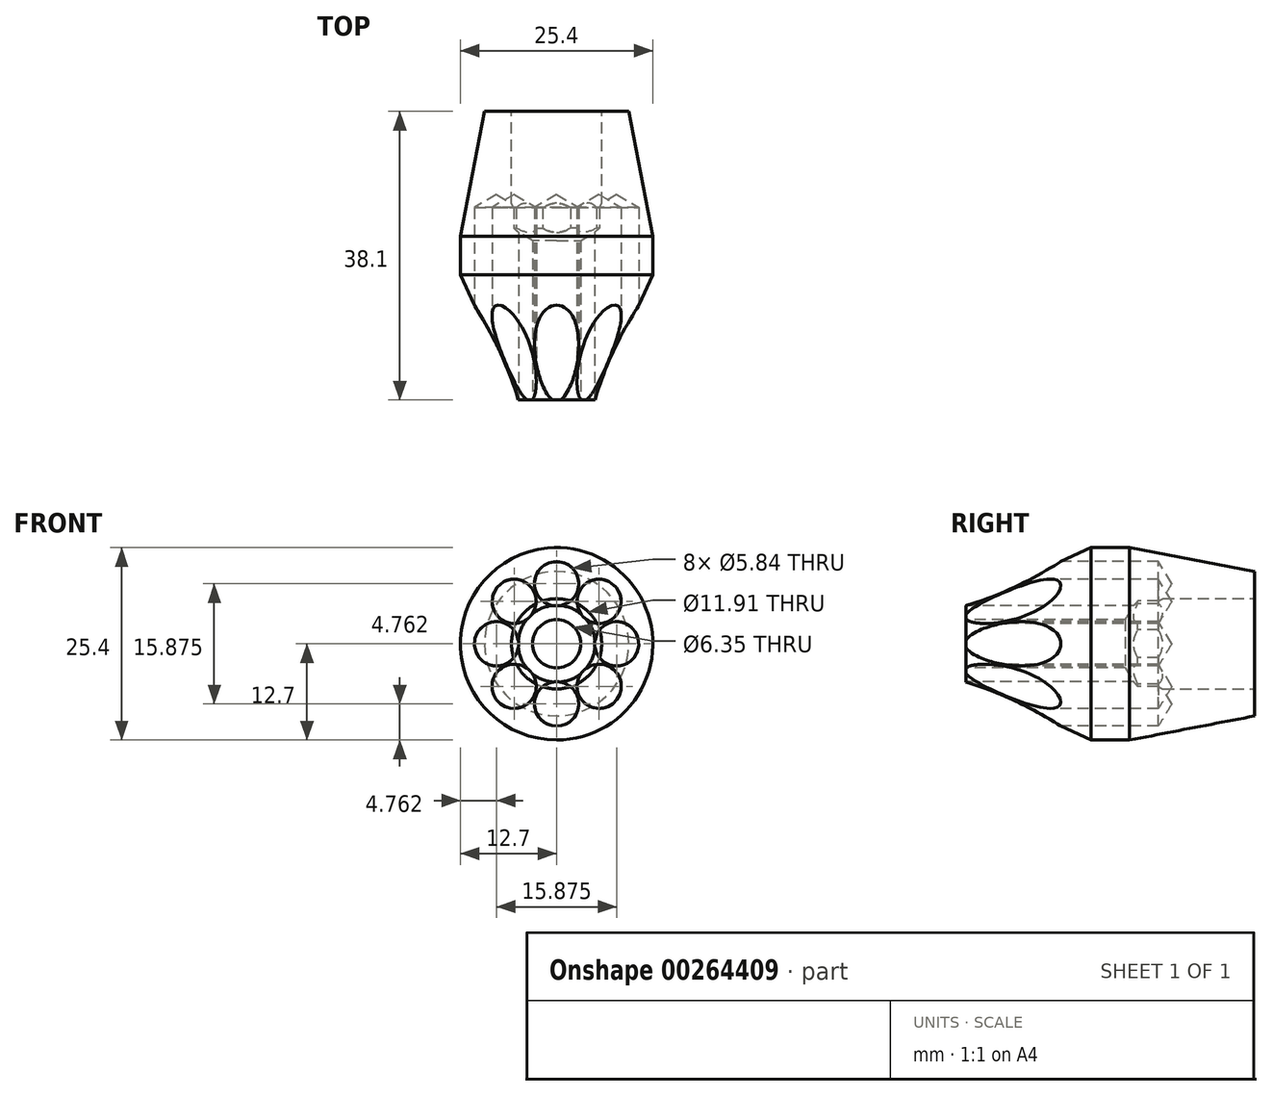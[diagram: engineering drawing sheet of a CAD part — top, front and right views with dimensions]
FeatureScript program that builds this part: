
annotation { "Feature Type Name" : "Feature", "Feature Type Description" : "" }
export const myFeature = defineFeature(function(context is Context, id is Id, definition is map)
    precondition{}
    {
        {
            var Q0;
            Q0=qCreatedBy(makeId("Front.planeOp"),FACE);
            var sketch = newSketch(context, id + "F0", { "sketchPlane" : qUnion([Q0])});
            skCircle(sketch, "E0", {"center": v(0, 0) * mm, "radius": 12.7 * mm});
            skSolve(sketch);
        }
        {
            var Q0;
            Q0 = qSketchRegion(id + "F0", true);
            extrude(context, id + "F1", {"entities" : qUnion([Q0]), "depth" : 38.1 * mm});
        }
        {
            var Q0;
            Q0=makeQuery(id+"F1.opExtrude","CAP_FACE",FACE,{"disambiguationData":[OSD([sQuery(id+"F0.wireOp",EDGE,"E0")])],"isStart":true});
            var sketch = newSketch(context, id + "F2", { "sketchPlane" : qUnion([Q0])});
            skPoint(sketch, "E1", {"position": v(0, 0) * mm});
            skSolve(sketch);
        }
        {
            var Q0;
            Q0=sQuery(id+"F2.wireOp",VERTEX,"E1");
            var Q1;
            Q1=makeQuery(id+"F1.opExtrude","SWEPT_BODY",BODY,{"disambiguationData":[OSD([sQuery(id+"F0.wireOp",EDGE,"E0")])]});
            hole(context, id + "F3", {"style" : HoleStyle.SIMPLE, "endStyle" : HoleEndStyle.BLIND, "standardTappedOrClearance" : lookupTablePath({ "standard" : "ANSI", "engagement" : "75%", "pitch" : "28 tpi", "size" : "1/2", "type" : "Tapped" }), "standardBlindInLast" : lookupTablePath({ "standard" : "ANSI", "engagement" : "75%", "pitch" : "28 tpi", "size" : "1/2", "type" : "Tapped" }), "holeDiameter" : 11.9 * mm, "showTappedDepth" : true, "holeDepth" : 15.42 * mm, "tappedDepth" : 12.7 * mm, "tapClearance" : 3, "locations" : qUnion([Q0]), "scope" : qUnion([Q1]), "majorDiameter" : 12.7 * mm});
        }
        {
            var Q0;
            Q0=makeQuery(id+"F1.opExtrude","CAP_FACE",FACE,{"disambiguationData":[OSD([sQuery(id+"F0.wireOp",EDGE,"E0")])],"isStart":false});
            var sketch = newSketch(context, id + "F4", { "sketchPlane" : qUnion([Q0])});
            skPoint(sketch, "E2", {"position": v(0, 0) * mm});
            skSolve(sketch);
        }
        {
            var Q0;
            Q0=sQuery(id+"F4.wireOp",VERTEX,"E2");
            var Q1;
            Q1=makeQuery(id+"F1.opExtrude","SWEPT_BODY",BODY,{"disambiguationData":[OSD([sQuery(id+"F0.wireOp",EDGE,"E0")])]});
            hole(context, id + "F5", {"style" : HoleStyle.SIMPLE, "endStyle" : HoleEndStyle.THROUGH, "holeDiameter" : 6.35 * mm, "tappedDepth" : 12.7 * mm, "tapClearance" : 3, "locations" : qUnion([Q0]), "scope" : qUnion([Q1])});
        }
        {
            var Q0;
            Q0=makeQuery(id+"F1.opExtrude","CAP_FACE",FACE,{"disambiguationData":[OSD([sQuery(id+"F0.wireOp",EDGE,"E0")])],"isStart":false});
            var sketch = newSketch(context, id + "F6", { "sketchPlane" : qUnion([Q0])});
            skLineSegment(sketch, "E3", {"start": v(0, 3.18) * mm, "end": v(0, 12.7) * mm});
            skCircle(sketch, "E4.cCircle", {"center": v(0, 0) * mm, "radius": 7.94 * mm, "construction": true});
            skLineSegment(sketch, "E4.0", {"start": v(0, 7.94) * mm, "end": v(5.61, 5.61) * mm});
            skLineSegment(sketch, "E4.1", {"start": v(5.61, 5.61) * mm, "end": v(7.94, 0) * mm});
            skLineSegment(sketch, "E4.2", {"start": v(7.94, 0) * mm, "end": v(5.61, -5.61) * mm});
            skLineSegment(sketch, "E4.3", {"start": v(5.61, -5.61) * mm, "end": v(0, -7.94) * mm});
            skLineSegment(sketch, "E4.4", {"start": v(0, -7.94) * mm, "end": v(-5.61, -5.61) * mm});
            skLineSegment(sketch, "E4.5", {"start": v(-5.61, -5.61) * mm, "end": v(-7.94, 0) * mm});
            skLineSegment(sketch, "E4.6", {"start": v(-7.94, 0) * mm, "end": v(-5.61, 5.61) * mm});
            skLineSegment(sketch, "E4.7", {"start": v(-5.61, 5.61) * mm, "end": v(0, 7.94) * mm});
            skSolve(sketch);
        }
        {
            var Q0;
            Q0=sQuery(id+"F6.wireOp",VERTEX,"E4.7.end");
            var Q1;
            Q1=sQuery(id+"F6.wireOp",VERTEX,"E4.7.start");
            var Q2;
            Q2=sQuery(id+"F6.wireOp",VERTEX,"E4.6.start");
            var Q3;
            Q3=sQuery(id+"F6.wireOp",VERTEX,"E4.5.start");
            var Q4;
            Q4=sQuery(id+"F6.wireOp",VERTEX,"E4.4.start");
            var Q5;
            Q5=sQuery(id+"F6.wireOp",VERTEX,"E4.3.start");
            var Q6;
            Q6=sQuery(id+"F6.wireOp",VERTEX,"E4.2.start");
            var Q7;
            Q7=sQuery(id+"F6.wireOp",VERTEX,"E4.1.start");
            var Q8;
            Q8=makeQuery(id+"F1.opExtrude","SWEPT_BODY",BODY,{"disambiguationData":[OSD([sQuery(id+"F0.wireOp",EDGE,"E0")])]});
            hole(context, id + "F7", {"style" : HoleStyle.SIMPLE, "endStyle" : HoleEndStyle.BLIND, "holeDiameter" : 5.84 * mm, "holeDepth" : 25.4 * mm, "tappedDepth" : 12.7 * mm, "tapClearance" : 3, "locations" : qUnion([Q0, Q1, Q2, Q3, Q4, Q5, Q6, Q7]), "scope" : qUnion([Q8])});
        }
        {
            var Q0;
            Q0=makeQuery(id+"F1.opExtrude","CAP_FACE",FACE,{"disambiguationData":[OSD([sQuery(id+"F0.wireOp",EDGE,"E0")])],"isStart":false});
            var sketch = newSketch(context, id + "F8", { "sketchPlane" : qUnion([Q0])});
            skCircle(sketch, "E5.cCircle", {"center": v(0, 0) * mm, "radius": 12.7 * mm, "construction": true});
            skLineSegment(sketch, "E5.0", {"start": v(4.86, 11.73) * mm, "end": v(11.73, 4.86) * mm});
            skLineSegment(sketch, "E5.1", {"start": v(11.73, 4.86) * mm, "end": v(11.73, -4.86) * mm});
            skLineSegment(sketch, "E5.2", {"start": v(11.73, -4.86) * mm, "end": v(4.86, -11.73) * mm});
            skLineSegment(sketch, "E5.3", {"start": v(4.86, -11.73) * mm, "end": v(-4.86, -11.73) * mm});
            skLineSegment(sketch, "E5.4", {"start": v(-4.86, -11.73) * mm, "end": v(-11.73, -4.86) * mm});
            skLineSegment(sketch, "E5.5", {"start": v(-11.73, -4.86) * mm, "end": v(-11.73, 4.86) * mm});
            skLineSegment(sketch, "E5.6", {"start": v(-11.73, 4.86) * mm, "end": v(-4.86, 11.73) * mm});
            skLineSegment(sketch, "E5.7", {"start": v(-4.86, 11.73) * mm, "end": v(4.86, 11.73) * mm});
            skSolve(sketch);
        }
        {
            var Q0;
            Q0=makeQuery(id+"F1.opExtrude","CAP_FACE",FACE,{"disambiguationData":[OSD([sQuery(id+"F0.wireOp",EDGE,"E0")])],"isStart":false});
            var sketch = newSketch(context, id + "F9", { "sketchPlane" : qUnion([Q0])});
            skCircle(sketch, "E6", {"center": v(0, 0) * mm, "radius": 5.02 * mm});
            skSolve(sketch);
        }
        {
            var Q0;
            {var subQ2=sQuery(id+"F0.wireOp",EDGE,"E0");var subQ8=makeQuery(id+"F1.opExtrude","CAP_EDGE",EDGE,{"disambiguationData":[OSD([subQ2])],"isStart":false});Q0=makeQuery(id+"F9.imprint","IMPRINT",FACE,{"disambiguationData":[TD([[makeQuery(id+"F9.imprint","IMPRINT",EDGE,{"derivedFrom":makeQuery(id+"Fwdx6luw1CHeDt6_1.hole-1.boolean.opBoolean","SPLIT",EDGE,{"disambiguationData":[OD(1.0)],"derivedFrom":subQ8})}),1.0]])]});}
            cPlane(context, id + "F10", {"entities" : qUnion([Q0]), "cplaneType" : CPlaneType.OFFSET, "offset" : 12.7 * mm, "oppositeDirection" : true, "width" : 152.4 * mm, "height" : 152.4 * mm});
        }
        {
            var Q0;
            Q0=makeQuery(id+"F1.opExtrude","CAP_EDGE",EDGE,{"disambiguationData":[OSD([sQuery(id+"F0.wireOp",EDGE,"E0")])],"isStart":false});
            chamfer(context, id + "F11", {"entities" : qUnion([Q0]), "chamferType" : ChamferType.TWO_OFFSETS, "width1" : 7.62 * mm, "oppositeDirection" : false, "width2" : 16.5 * mm, "tangentPropagation" : true});
        }
        {
            var Q0;
            Q0=makeQuery(id+"F1.opExtrude","CAP_EDGE",EDGE,{"disambiguationData":[OSD([sQuery(id+"F0.wireOp",EDGE,"E0")])],"isStart":true});
            chamfer(context, id + "F12", {"entities" : qUnion([Q0]), "chamferType" : ChamferType.TWO_OFFSETS, "width1" : 16.5 * mm, "oppositeDirection" : false, "width2" : 3.17 * mm, "tangentPropagation" : true});
        }
    });
